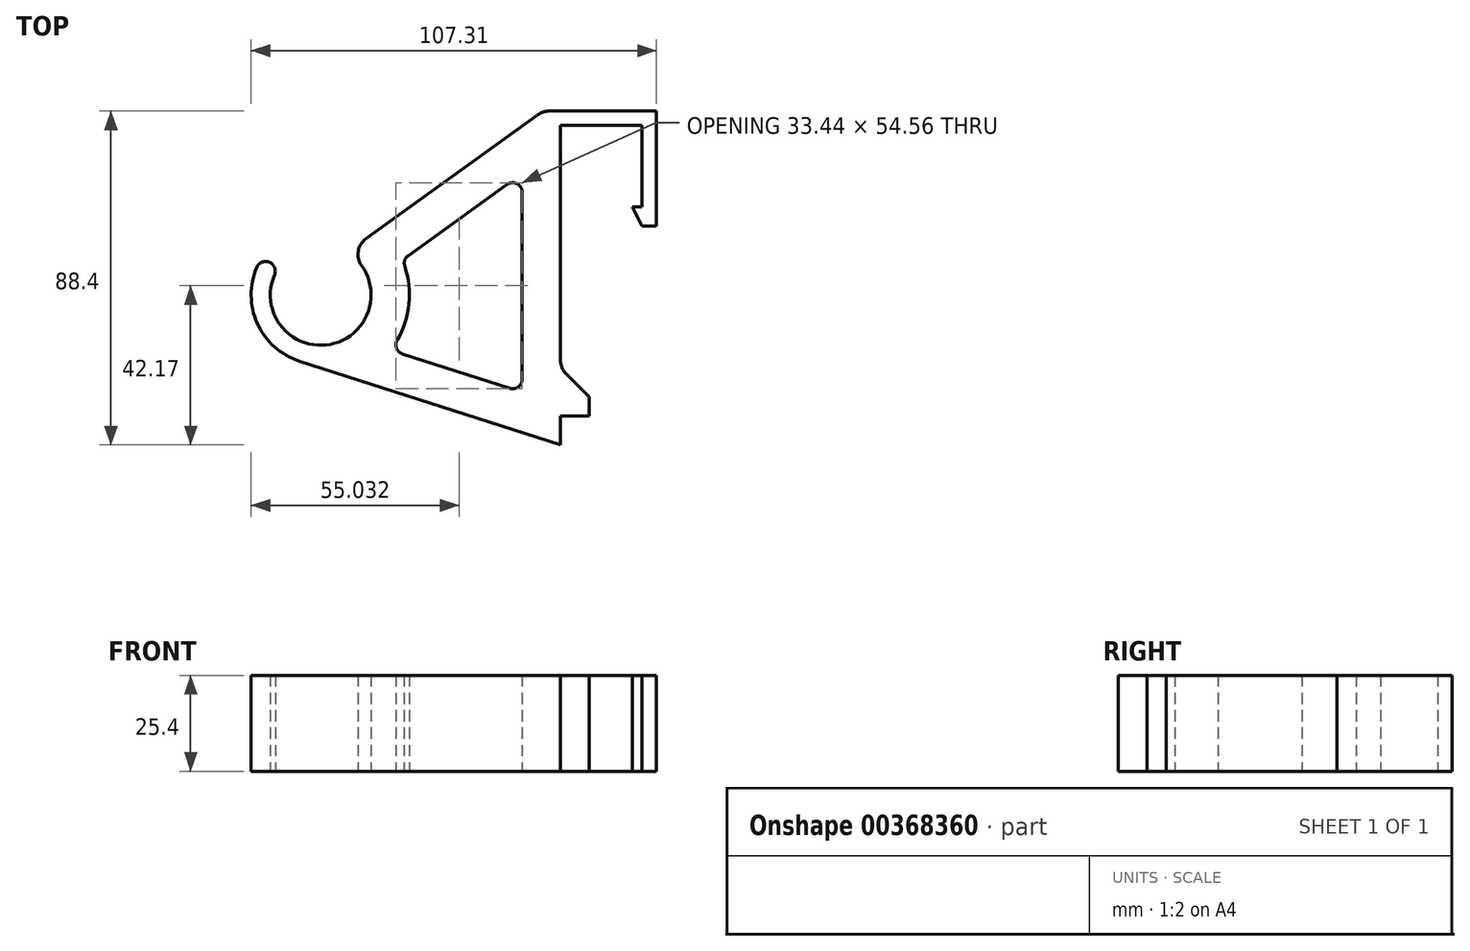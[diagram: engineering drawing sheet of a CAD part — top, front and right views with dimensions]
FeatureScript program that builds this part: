
annotation { "Feature Type Name" : "Feature", "Feature Type Description" : "" }
export const myFeature = defineFeature(function(context is Context, id is Id, definition is map)
    precondition{}
    {
        {
            var Q0;
            Q0=qCreatedBy(makeId("Top.planeOp"),FACE);
            var sketch = newSketch(context, id + "F0", { "sketchPlane" : qUnion([Q0])});
            skLineSegment(sketch, "E0", {"start": v(0, 73.03) * mm, "end": v(0, 10.87) * mm});
            skLineSegment(sketch, "E1", {"start": v(7.62, 1.14) * mm, "end": v(7.62, -3.94) * mm});
            skLineSegment(sketch, "E2", {"start": v(7.62, -3.94) * mm, "end": v(0, -3.94) * mm});
            skLineSegment(sketch, "E3", {"start": v(0, -3.94) * mm, "end": v(0, -11.56) * mm});
            skLineSegment(sketch, "E4", {"start": v(0, -11.56) * mm, "end": v(-69.13, 10.65) * mm});
            skArc(sketch, "E5", {"start": v(-75.74, 33.47) * mm, "mid": v(-62.07, 14.93) * mm, "end": v(-52.67, 35.97) * mm});
            skLineSegment(sketch, "E6", {"start": v(0, 73.03) * mm, "end": v(21.6, 73.03) * mm});
            skLineSegment(sketch, "E7", {"start": v(21.6, 73.03) * mm, "end": v(21.6, 51.44) * mm});
            skLineSegment(sketch, "E8", {"start": v(21.6, 51.44) * mm, "end": v(19.05, 51.44) * mm});
            skLineSegment(sketch, "E9", {"start": v(19.05, 51.44) * mm, "end": v(21.6, 46.36) * mm});
            skLineSegment(sketch, "E10", {"start": v(21.6, 46.36) * mm, "end": v(25.4, 46.36) * mm});
            skLineSegment(sketch, "E11", {"start": v(25.4, 46.36) * mm, "end": v(25.4, 76.83) * mm});
            skLineSegment(sketch, "E12", {"start": v(25.4, 76.83) * mm, "end": v(-2.97, 76.83) * mm});
            skLineSegment(sketch, "E13", {"start": v(-5.94, 75.88) * mm, "end": v(-51.52, 43.05) * mm});
            skArc(sketch, "E14", {"start": v(-80.4, 35.49) * mm, "mid": v(-80.27, 20.57) * mm, "end": v(-69.13, 10.65) * mm});
            skArc(sketch, "E15", {"start": v(-80.4, 35.49) * mm, "mid": v(-77.07, 36.81) * mm, "end": v(-75.74, 33.47) * mm});
            skPoint(sketch, "E16.visualSharp", {"position": v(-56.45, 39.5) * mm});
            skArc(sketch, "E16.filletArc", {"start": v(-51.52, 43.05) * mm, "mid": v(-53.56, 39.75) * mm, "end": v(-52.67, 35.97) * mm});
            skLineSegment(sketch, "E17", {"start": v(7.62, 1.14) * mm, "end": v(1.49, 7.28) * mm});
            skPoint(sketch, "E18.start.orphan", {"position": v(0, 0) * mm});
            skPoint(sketch, "E19.visualSharp", {"position": v(-4.61, 76.83) * mm});
            skArc(sketch, "E19.filletArc", {"start": v(-2.97, 76.83) * mm, "mid": v(-4.53, 76.59) * mm, "end": v(-5.94, 75.88) * mm});
            skPoint(sketch, "E20.visualSharp", {"position": v(0, 8.76) * mm});
            skArc(sketch, "E20.filletArc", {"start": v(0, 10.87) * mm, "mid": v(0.39, 8.92) * mm, "end": v(1.49, 7.28) * mm});
            skLineSegment(sketch, "E21", {"start": v(-10.16, 55.36) * mm, "end": v(-10.16, 5.86) * mm});
            skLineSegment(sketch, "E22", {"start": v(-13.48, 3.44) * mm, "end": v(-41.84, 12.56) * mm});
            skLineSegment(sketch, "E23", {"start": v(-14.18, 57.42) * mm, "end": v(-40.32, 38.6) * mm});
            skArc(sketch, "E24", {"start": v(-43.25, 16.26) * mm, "mid": v(-40.13, 25.77) * mm, "end": v(-41.25, 35.72) * mm});
            skPoint(sketch, "E25.visualSharp", {"position": v(-10.16, 60.32) * mm});
            skArc(sketch, "E25.filletArc", {"start": v(-10.16, 55.36) * mm, "mid": v(-11.54, 57.62) * mm, "end": v(-14.18, 57.42) * mm});
            skPoint(sketch, "E26.visualSharp", {"position": v(-10.16, 2.38) * mm});
            skArc(sketch, "E26.filletArc", {"start": v(-13.48, 3.44) * mm, "mid": v(-11.2, 3.8) * mm, "end": v(-10.16, 5.86) * mm});
            skPoint(sketch, "E27.visualSharp", {"position": v(-45.08, 13.6) * mm});
            skArc(sketch, "E27.filletArc", {"start": v(-43.25, 16.26) * mm, "mid": v(-43.44, 14.07) * mm, "end": v(-41.84, 12.56) * mm});
            skPoint(sketch, "E28.visualSharp", {"position": v(-41.9, 37.45) * mm});
            skArc(sketch, "E28.filletArc", {"start": v(-40.32, 38.6) * mm, "mid": v(-41.26, 37.3) * mm, "end": v(-41.25, 35.72) * mm});
            skSolve(sketch);
        }
        {
            var Q0;
            Q0 = qSketchRegion(id + "F0", true);
            extrude(context, id + "F1", {"entities" : qUnion([Q0]), "depth" : 25.4 * mm});
        }
    });
